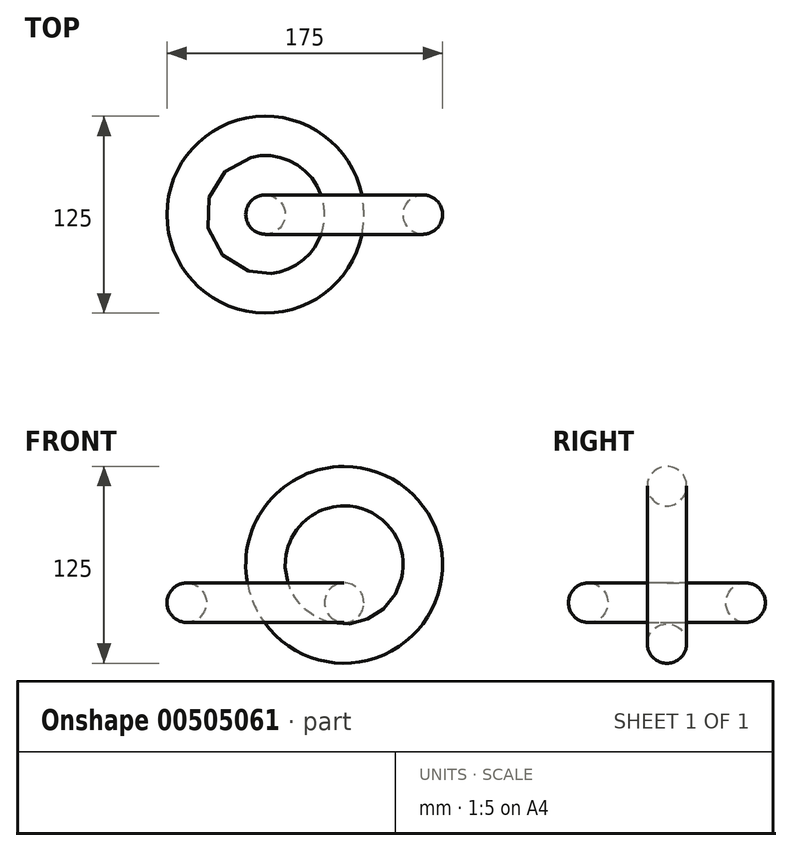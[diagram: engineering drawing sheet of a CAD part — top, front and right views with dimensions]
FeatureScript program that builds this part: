
annotation { "Feature Type Name" : "Feature", "Feature Type Description" : "" }
export const myFeature = defineFeature(function(context is Context, id is Id, definition is map)
    precondition{}
    {
        {
            var Q0;
            Q0=qCreatedBy(makeId("Front.planeOp"),FACE);
            var sketch = newSketch(context, id + "F0", { "sketchPlane" : qUnion([Q0])});
            skLineSegment(sketch, "E0", {"start": v(0, 13.47) * mm, "end": v(0, -13.9) * mm});
            skLineSegment(sketch, "E1", {"start": v(-50, 0) * mm, "end": v(0, 0) * mm, "construction": true});
            skLineSegment(sketch, "E2", {"start": v(-50, -24) * mm, "end": v(-50, 0) * mm, "construction": true});
            skCircle(sketch, "E3", {"center": v(-50, -24) * mm, "radius": 12.5 * mm});
            skSolve(sketch);
        }
        {
            var Q0;
            Q0=makeQuery(id+"F0.imprint","IMPRINT",FACE,{"disambiguationData":[TD([[makeQuery(id+"F0.imprint","IMPRINT",EDGE,{"derivedFrom":sQuery(id+"F0.wireOp",EDGE,"Nx3AAZYy-8eBW-LlQo-tXD7-DuzKIJajSmD5")}),1.0]])]});
            var Q1;
            Q1=makeQuery(id+"F0.imprint","IMPRINT",FACE,{"disambiguationData":[TD([[makeQuery(id+"F0.imprint","IMPRINT",EDGE,{"derivedFrom":sQuery(id+"F0.wireOp",EDGE,"E3")}),1.0]])]});
            var Q2;
            Q2=sQuery(id+"F0.wireOp",EDGE,"E0");
            revolve(context, id + "F1", {"entities" : qUnion([Q0, Q1]), "axis" : qUnion([Q2]), "revolveType" : RevolveType.FULL});
        }
        {
            var Q0;
            Q0=qCreatedBy(makeId("Top.planeOp"),FACE);
            var sketch = newSketch(context, id + "F2", { "sketchPlane" : qUnion([Q0])});
            skCircle(sketch, "E4", {"center": v(0, 0) * mm, "radius": 12.5 * mm});
            skLineSegment(sketch, "E5", {"start": v(0, 0) * mm, "end": v(50, 0) * mm, "construction": true});
            skLineSegment(sketch, "E6", {"start": v(50, 0) * mm, "end": v(50, -11.2) * mm});
            skSolve(sketch);
        }
        {
            var Q0;
            Q0=makeQuery(id+"F2.imprint","IMPRINT",FACE,{"disambiguationData":[TD([[makeQuery(id+"F2.imprint","IMPRINT",EDGE,{"derivedFrom":sQuery(id+"F2.wireOp",EDGE,"E4")}),1.0]])]});
            var Q1;
            Q1=sQuery(id+"F2.wireOp",EDGE,"E6");
            revolve(context, id + "F3", {"entities" : qUnion([Q0]), "axis" : qUnion([Q1]), "revolveType" : RevolveType.FULL});
        }
    });
